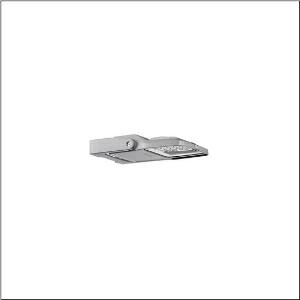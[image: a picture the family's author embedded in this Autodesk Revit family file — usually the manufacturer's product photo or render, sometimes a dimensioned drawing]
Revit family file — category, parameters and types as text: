
# Revit family: floodlight_fl_21_iq_micro___pl43_5xa7762a4a2a_306a
name_source: partatom
category: Lighting Fixtures
units: mm (PartAtom-declared; Revit-internal decimal feet)

## family parameters
Cut with Voids When Loaded = No
Host = Face
Light Source = No
Part Type = Normal
Room Calculation Point = No
Round Connector Dimension = Use Diameter
Shared = No

## types (1)
- --- (1 x LED, 3170 lm, 23.1 W, 4000K)
    Apparent Load = 23 VA
    CIE Flux Codes = 29 80 99 100 100
    Color Rendering = 70
    Color Temperature = 4000K
    Default Elevation = 1800 mm
    Description = Floodlight FL 21 iQ micro, floodlight, primary light control with lens, of PMMA, primary optical cover: protective disc, of toughened safety glass, transparent, light distribution: PL43, light emission: direct distribution, installation type: surface-mounted, LED, High Power LED, rated luminous flux: 3.170lm, luminous efficacy: 137lm/W, light colour: 740, colour temperature: 4000K, control: Auto-Match, Temp-Guard, Night-Set, Smart-Wire, Desk-Remote (wireless, voltage-free reading and setting of iQ features in the workshop via application-optimized NFC function/RFID function), optimised constant luminous flux control (CLO 2.0), Street-Remote, with terminal, 6-pole, mains connection: 220..240V, AC, 50/60Hz, start of lifetime: 23W, end of service life: 24W, reduction: 11W, luminaire housing, of diecast aluminium, powder-coated, Siteco® metallic grey (DB 702S), corrosivity category C5 mid according to DIN EN ISO 12944, sealing non-destructively replaceable, design bracket, of diecast aluminium, powder-coated, Siteco® metallic grey (DB 702S), protection rating (complete): IP66, insulation class (complete): insulation class II (safety insulation), certification: CE, ENEC, VDE, protection symbol: D, impact resistance: IK07, permissible operating ambient temperature: -40..+40°C, permissible operating ambient temperature for outdoor applications: -40..+50°C, standard: DIN EN 12944, LABS conformity tested according to VDMA 24364:2018-05, packaging unit: 1 piece

Light Distribution: PL43
    Height = 65 mm
    Lamp = 1 x LED
    Lamp Light Flux = 3170 lm
    Lamp Power = 23.1 W
    Lamp count = 1
    Length = 312 mm
    Luminous efficacy = 137 lm/W
    Manufacturer = Siteco
    ModVariant = No
    Model = 5XA7762A4A2A
    Mounting Place = Wall
    Mounting Type = Surface mounted
    Number of Poles = 1
    OnlyDefault = Yes
    Power Factor = 1
    Product Name = Floodlight FL 21 iQ micro | PL43
    Product group = floodlight | wall mounted
    ProductGroupID = 2001
    Protection Class = Protection class II
    Protection Degree = IP 66
    RLX_Detail_Level = 1
    RLX_Emergency_Light_Flux = 0 lm
    RLX_Emergency_Type = 0
    RLX_Emergency_Type_DB = No
    RlxData = <blob elided: 97373 chars, md5=69c5f1f5>
    Socket = socket
    Standby Power = 0 W
    System Light Flux = 3170 lm
    System Power = 23 W
    Type Comments = factory setting: luminous flux: 100 % | dim-lin: 254 | 455 mA
    Type Image = l_1006878.jpg
    URL = http://relux.com
    VarID = @adj_109877
    Voltage = 0 V
    Weight = 0.00 kg
    Width = 230 mm

## geometry (parser evidence)
native form markers: Blend x4, Sweep x11
no freeform markers — native parametric forms only
